# Revit family: FU_Config_Sandler_Kern 0360
name_source: partatom
category: Furniture
units: mm (PartAtom-declared; Revit-internal decimal feet)

## family parameters
Always vertical = Yes
Cut with Voids When Loaded = No
OmniClass Number = 23.40.20.00
OmniClass Title = General Furniture and Specialties
Render Appearance Source = Family Geometry
Room Calculation Point = No
Shared = No
Work Plane-Based = No

## types (1)
- Kern 3060
    Default Elevation = 0 mm  [stored 0 ft]
    Depth = 1480 mm  [stored 4.85564 ft]
    Description = Room Configuration 6: a four-seat room with privacy screens on three sides. Consists of 2 two-seaters with backrests and armrests on the ends (KER0242 and KER0244), 2 rear panels (KER1242PC and KER1244PC), and 1 narrow connecting panel (KER2070). 82.7"/210cm wide, 58.3"/148cm deep.
    Height = 1260 mm  [stored 4.13386 ft]
    Manufacturer = Sandler
    Model = Kern 3060
    Panel = Fabric - Mainline Flax - Bayswater MLF24
    URL = https://www.sandlerseating.com
    Width = 2070 mm  [stored 6.79134 ft]

note: [stored X ft] marks values corroborated as IEEE doubles in the binary element streams (Revit-internal decimal feet)

## geometry (parser evidence)
native form markers: Sweep x31
no freeform markers — native parametric forms only
